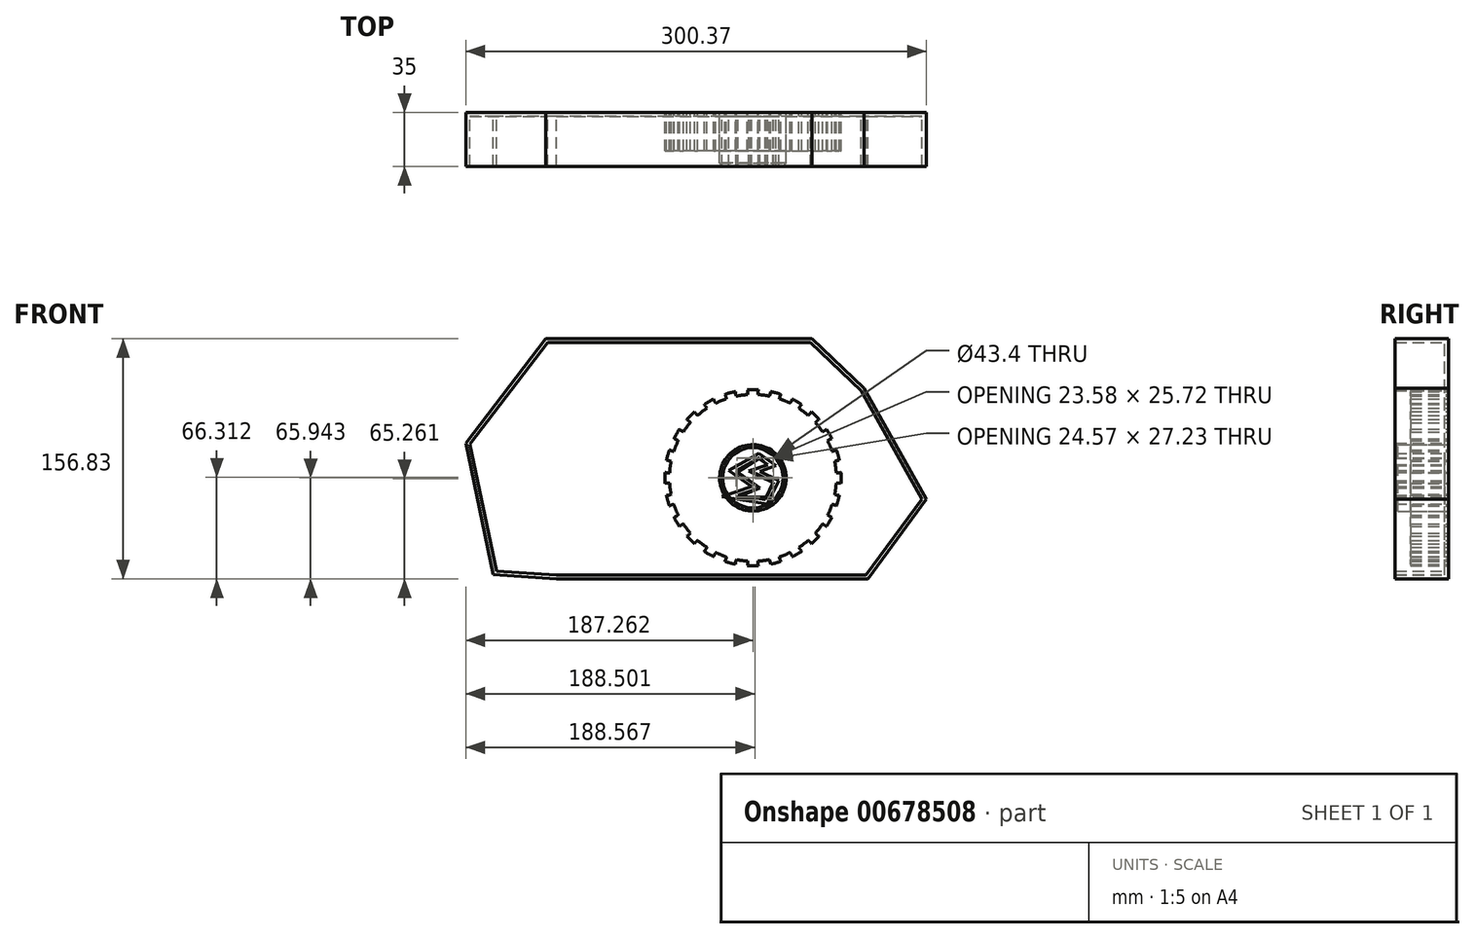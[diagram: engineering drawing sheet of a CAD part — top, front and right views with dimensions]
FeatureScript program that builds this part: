
annotation { "Feature Type Name" : "Feature", "Feature Type Description" : "" }
export const myFeature = defineFeature(function(context is Context, id is Id, definition is map)
    precondition{}
    {
        {
            var Q0;
            Q0=qCreatedBy(makeId("Front.planeOp"),FACE);
            var sketch = newSketch(context, id + "F0", { "sketchPlane" : qUnion([Q0])});
            skArc(sketch, "E0", {"start": v(1.86, 25.51) * mm, "mid": v(0.1, 25.48) * mm, "end": v(-1.65, 25.4) * mm, "construction": true});
            skCircle(sketch, "E1", {"center": v(1.86, -28.2) * mm, "radius": 58.67 * mm, "construction": true});
            skCircle(sketch, "E2", {"center": v(1.86, -28.2) * mm, "radius": 63.5 * mm, "construction": true});
            skLineSegment(sketch, "E3", {"start": v(1.86, -28.2) * mm, "end": v(1.86, 47.81) * mm, "construction": true});
            skLineSegment(sketch, "E4", {"start": v(1.86, -28.2) * mm, "end": v(-3.19, 48.87) * mm, "construction": true});
            skLineSegment(sketch, "E5", {"start": v(-13.23, 27.28) * mm, "end": v(-16.07, 26.5) * mm, "construction": true});
            skArc(sketch, "E6", {"start": v(-16.05, 26.44) * mm, "mid": v(18.37, -83.3) * mm, "end": v(-13.23, 27.28) * mm, "construction": true});
            skArc(sketch, "E7", {"start": v(1.86, 7.25) * mm, "mid": v(0.7, 7.23) * mm, "end": v(-0.46, 7.17) * mm});
            skArc(sketch, "E8", {"start": v(59.37, -28.2) * mm, "mid": v(36.78, 17.48) * mm, "end": v(-13.23, 27.28) * mm});
            skCircle(sketch, "E9", {"center": v(1.86, -28.2) * mm, "radius": 54.44 * mm});
            skCircle(sketch, "E10", {"center": v(-1.98, 30.34) * mm, "radius": 14.6 * mm, "construction": true});
            skLineSegment(sketch, "E11", {"start": v(1.83, 30.47) * mm, "end": v(-38.04, 35.66) * mm, "construction": true});
            skLineSegment(sketch, "E12", {"start": v(1.83, 30.47) * mm, "end": v(-35.46, 22.15) * mm, "construction": true});
            skArc(sketch, "E13.trimOffspring", {"start": v(-1.71, 29.19) * mm, "mid": v(-1.91, 30.1) * mm, "end": v(-2.17, 30.99) * mm, "construction": true});
            skArc(sketch, "E14.trimOffspring", {"start": v(-1.6, 24.55) * mm, "mid": v(-1.51, 25.34) * mm, "end": v(-1.47, 26.13) * mm, "construction": true});
            skArc(sketch, "E15.trimOffspring", {"start": v(-29.7, 21.26) * mm, "mid": v(-29.47, 20.7) * mm, "end": v(-29.23, 20.17) * mm, "construction": true});
            skCircle(sketch, "E16", {"center": v(-16.05, 26.44) * mm, "radius": 14.6 * mm, "construction": true});
            skArc(sketch, "E17", {"start": v(-1.71, 29.19) * mm, "mid": v(-2.57, 32.26) * mm, "end": v(-4.22, 35) * mm});
            skArc(sketch, "E18", {"start": v(-1.65, 25.4) * mm, "mid": v(-1.43, 27.3) * mm, "end": v(-1.71, 29.19) * mm});
            skPoint(sketch, "E19.orphan", {"position": v(7.94, 35) * mm});
            skPoint(sketch, "E20.MirrorCS.start.orphan", {"position": v(5.44, 29.19) * mm});
            skPoint(sketch, "E21.MirrorCS.start.orphan", {"position": v(5.38, 25.4) * mm});
            skArc(sketch, "E22.MirrorCS", {"start": v(5.38, 25.4) * mm, "mid": v(5.15, 27.3) * mm, "end": v(5.44, 29.19) * mm});
            skCircle(sketch, "E23", {"center": v(1.86, -28.2) * mm, "radius": 33.92 * mm});
            skCircle(sketch, "E24", {"center": v(1.86, -28.2) * mm, "radius": 21.7 * mm});
            skLineSegment(sketch, "E25", {"start": v(1.86, -12.48) * mm, "end": v(0.83, -12.48) * mm});
            skPoint(sketch, "E26.start.orphan", {"position": v(-16.93, -28.2) * mm});
            skPoint(sketch, "E27.start.orphan", {"position": v(19.92, -28.2) * mm});
            skPoint(sketch, "E28.end.orphan", {"position": v(-3.1, -7.08) * mm});
            skPoint(sketch, "E29.orphan", {"position": v(-3.1, -12.48) * mm});
            skLineSegment(sketch, "E30", {"start": v(6.38, -14.98) * mm, "end": v(-8.62, -24.62) * mm});
            skLineSegment(sketch, "E31", {"start": v(-8.62, -24.62) * mm, "end": v(6.38, -34.8) * mm});
            skLineSegment(sketch, "E32", {"start": v(6.38, -34.8) * mm, "end": v(-8.09, -40.7) * mm});
            skLineSegment(sketch, "E33", {"start": v(-8.09, -40.7) * mm, "end": v(10.4, -40.7) * mm});
            skLineSegment(sketch, "E34", {"start": v(10.4, -40.7) * mm, "end": v(14.96, -31.32) * mm});
            skLineSegment(sketch, "E35", {"start": v(14.96, -31.32) * mm, "end": v(-0.85, -23.82) * mm});
            skLineSegment(sketch, "E36", {"start": v(-0.85, -23.82) * mm, "end": v(11.2, -19.8) * mm});
            skLineSegment(sketch, "E37", {"start": v(11.2, -19.8) * mm, "end": v(6.38, -14.98) * mm});
            skSolve(sketch);
        }
        {
            var Q0;
            Q0=makeQuery(id+"F0.imprint","IMPRINT",FACE,{"disambiguationData":[TD([[makeQuery(id+"F0.imprint","IMPRINT",EDGE,{"derivedFrom":sQuery(id+"F0.wireOp",EDGE,"E23")}),-1.0]])]});
            var Q1;
            Q1=makeQuery(id+"F0.imprint","IMPRINT",FACE,{"disambiguationData":[TD([[makeQuery(id+"F0.imprint","IMPRINT",EDGE,{"derivedFrom":sQuery(id+"F0.wireOp",EDGE,"E23")}),1.0]])]});
            var Q2;
            {var subQ0=sQuery(id+"F0.wireOp",EDGE,"E18");var subQ1=sQuery(id+"F0.wireOp",EDGE,"E8");var subQ2=makeQuery(id+"F0.imprint","INTERSECT",VERTEX,{"derivedFrom":[subQ1,subQ0]});Q2=makeQuery(id+"F0.imprint","IMPRINT",FACE,{"disambiguationData":[TD([[makeQuery(id+"F0.imprint","IMPRINT",EDGE,{"disambiguationData":[TD([[subQ2,1.0]])],"derivedFrom":subQ1}),1.0]])]});}
            extrude(context, id + "F1", {"entities" : qUnion([Q0, Q1, Q2]), "depth" : 25 * mm, "offsetDistance" : 25 * mm});
        }
        {
            var Q0;
            Q0=makeQuery(id+"F1.opExtrude","SWEPT_BODY",BODY,{"disambiguationData":[OSD([sQuery(id+"F0.wireOp",EDGE,"E8"),sQuery(id+"F0.wireOp",EDGE,"E9"),sQuery(id+"F0.wireOp",EDGE,"E18"),sQuery(id+"F0.wireOp",EDGE,"E22.MirrorCS"),sQuery(id+"F0.wireOp",EDGE,"E24")])]});
            var Q1;
            Q1=makeQuery(id+"F1.opExtrude","SWEPT_FACE",FACE,{"disambiguationData":[OSD([sQuery(id+"F0.wireOp",EDGE,"E9")])]});
            circularPattern(context, id + "F2", {"operationType" : NewBodyOperationType.ADD, "entities" : qUnion([Q0]), "axis" : qUnion([Q1]), "angle" : 360 * degree, "instanceCount" : 24, "equalSpace" : true});
        }
        {
            var Q0;
            Q0=makeQuery(id+"F0.imprint","IMPRINT",FACE,{"disambiguationData":[TD([[makeQuery(id+"F0.imprint","IMPRINT",EDGE,{"derivedFrom":sQuery(id+"F0.wireOp",EDGE,"E24")}),1.0]])]});
            extrude(context, id + "F3", {"entities" : qUnion([Q0]), "depth" : 35 * mm, "offsetDistance" : 25 * mm});
        }
        {
            var Q0;
            Q0=makeQuery(id+"F3.opExtrude","CAP_EDGE",EDGE,{"disambiguationData":[OSD([sQuery(id+"F0.wireOp",EDGE,"E24")])],"isStart":false});
            chamfer(context, id + "F4", {"entities" : qUnion([Q0]), "width" : 2 * mm, "tangentPropagation" : true});
        }
        {
            var Q0;
            Q0=qCreatedBy(makeId("Front.planeOp"),FACE);
            var sketch = newSketch(context, id + "F5", { "sketchPlane" : qUnion([Q0])});
            skLineSegment(sketch, "E38", {"start": v(-74.71, -94.15) * mm, "end": v(77.03, -94.15) * mm});
            skLineSegment(sketch, "E39", {"start": v(77.03, -94.15) * mm, "end": v(114.97, -42.14) * mm});
            skLineSegment(sketch, "E40", {"start": v(114.97, -42.14) * mm, "end": v(74.3, 30.21) * mm});
            skLineSegment(sketch, "E41", {"start": v(74.3, 30.21) * mm, "end": v(40.27, 62.68) * mm});
            skLineSegment(sketch, "E42", {"start": v(40.27, 62.68) * mm, "end": v(-73.54, 62.68) * mm});
            skLineSegment(sketch, "E43", {"start": v(-73.54, 62.68) * mm, "end": v(-133.37, 62.68) * mm});
            skLineSegment(sketch, "E44", {"start": v(-126.34, -94.15) * mm, "end": v(-74.71, -94.15) * mm});
            skLineSegment(sketch, "E45", {"start": v(-126.34, -94.15) * mm, "end": v(-167.47, -91.38) * mm});
            skLineSegment(sketch, "E46", {"start": v(-167.47, -91.38) * mm, "end": v(-185.4, -5.73) * mm});
            skLineSegment(sketch, "E47", {"start": v(-185.4, -5.73) * mm, "end": v(-133.37, 62.68) * mm});
            skLineSegment(sketch, "E48", {"start": v(11.43, -19.43) * mm, "end": v(5.56, -15.27) * mm});
            skLineSegment(sketch, "E49", {"start": v(5.56, -15.27) * mm, "end": v(-9.19, -23.56) * mm});
            skLineSegment(sketch, "E50", {"start": v(-9.19, -23.56) * mm, "end": v(6.44, -34.7) * mm});
            skLineSegment(sketch, "E51", {"start": v(6.44, -34.7) * mm, "end": v(-8.03, -39.6) * mm});
            skLineSegment(sketch, "E52", {"start": v(-8.03, -39.6) * mm, "end": v(9.8, -42.5) * mm});
            skLineSegment(sketch, "E53", {"start": v(9.8, -42.5) * mm, "end": v(15.39, -31.08) * mm});
            skLineSegment(sketch, "E54", {"start": v(15.39, -31.08) * mm, "end": v(0, -23.56) * mm});
            skLineSegment(sketch, "E55", {"start": v(0, -23.56) * mm, "end": v(11.43, -19.43) * mm});
            skSolve(sketch);
        }
        {
            var Q0;
            Q0=makeQuery(id+"F5.imprint","IMPRINT",FACE,{"disambiguationData":[TD([[makeQuery(id+"F5.imprint","IMPRINT",EDGE,{"derivedFrom":sQuery(id+"F5.wireOp",EDGE,"E38")}),1.0]])]});
            extrude(context, id + "F6", {"entities" : qUnion([Q0]), "depth" : 35 * mm, "offsetDistance" : 25 * mm});
        }
        {
            var Q0;
            Q0=makeQuery(id+"F6.opExtrude","CAP_FACE",FACE,{"disambiguationData":[OSD([sQuery(id+"F5.wireOp",EDGE,"E38"),sQuery(id+"F5.wireOp",EDGE,"E39"),sQuery(id+"F5.wireOp",EDGE,"E40"),sQuery(id+"F5.wireOp",EDGE,"E41"),sQuery(id+"F5.wireOp",EDGE,"E42"),sQuery(id+"F5.wireOp",EDGE,"E43"),sQuery(id+"F5.wireOp",EDGE,"FSdbT221-Z7ds-3vMY-kbvv-MHOY6NPJU1vu"),sQuery(id+"F5.wireOp",EDGE,"KNYzKmaq-yceu-U5Oh-dX3I-7wkiPAD7Isrz"),sQuery(id+"F5.wireOp",EDGE,"E44")])],"isStart":false});
            shell(context, id + "F7", {"entities" : qUnion([Q0]), "thickness" : 2.5 * mm});
        }
    });
